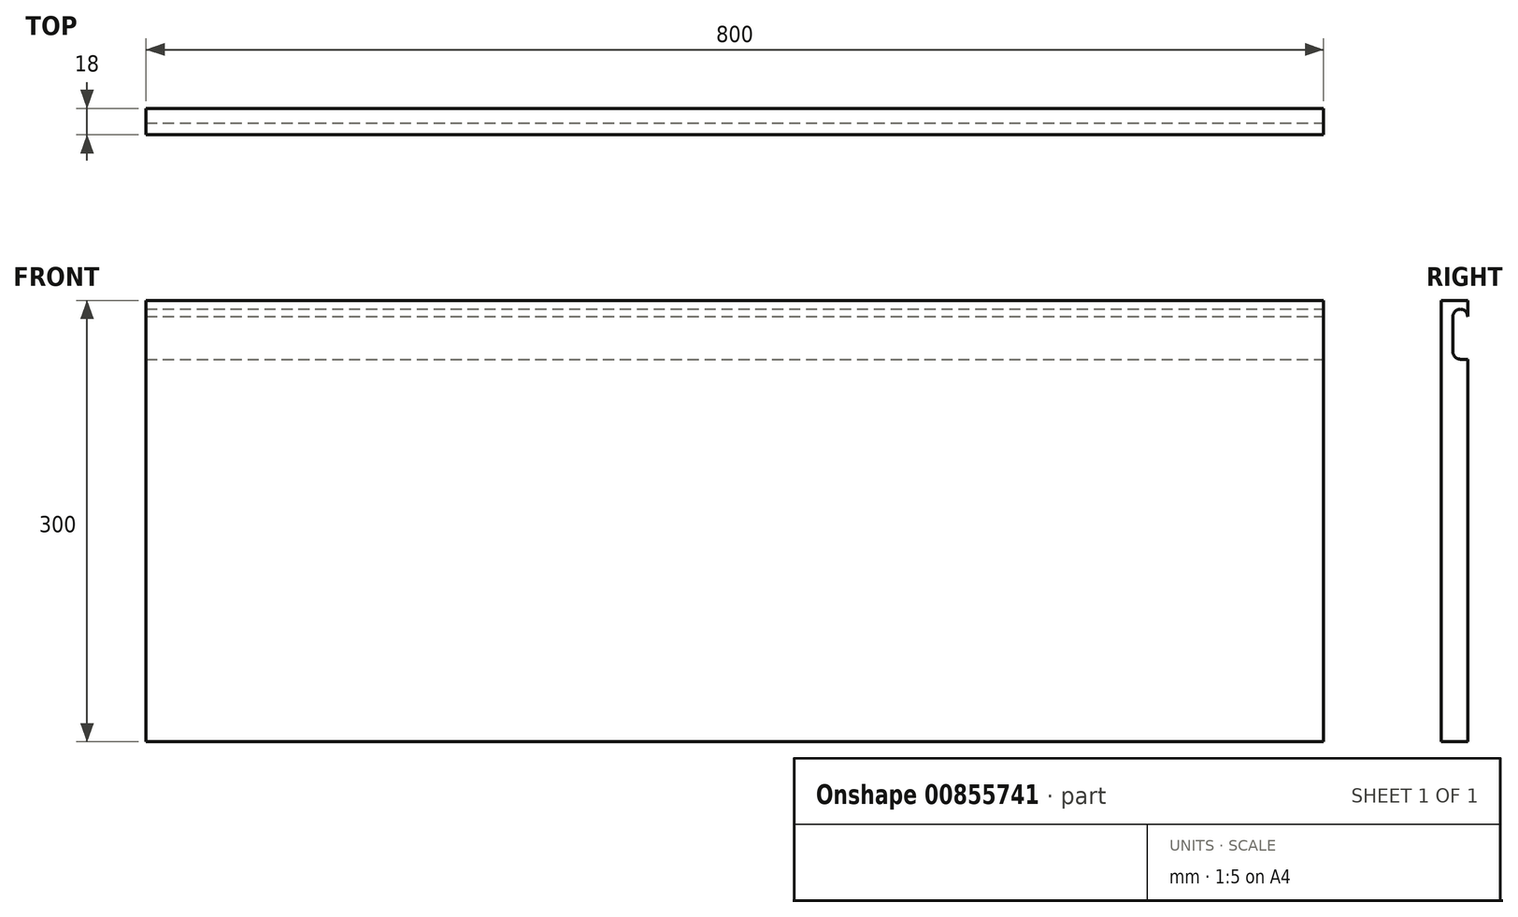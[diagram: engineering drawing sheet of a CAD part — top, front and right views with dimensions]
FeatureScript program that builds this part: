
annotation { "Feature Type Name" : "Feature", "Feature Type Description" : "" }
export const myFeature = defineFeature(function(context is Context, id is Id, definition is map)
    precondition{}
    {
        {
            var Q0;
            Q0=qCreatedBy(makeId("Front.planeOp"),FACE);
            var sketch = newSketch(context, id + "F0", { "sketchPlane" : qUnion([Q0])});
            skLineSegment(sketch, "E0.0", {"start": v(-303.71, 131.37) * mm, "end": v(-303.71, -87.91) * mm});
            skLineSegment(sketch, "E0.1", {"start": v(-303.71, -87.91) * mm, "end": v(-303.71, -150.63) * mm});
            skLineSegment(sketch, "E0.5", {"start": v(-303.71, 131.37) * mm, "end": v(53.29, 131.37) * mm});
            skLineSegment(sketch, "E1.1", {"start": v(460.29, 131.37) * mm, "end": v(460.29, -150.63) * mm});
            skLineSegment(sketch, "E1.2", {"start": v(53.29, 131.37) * mm, "end": v(460.29, 131.37) * mm});
            skLineSegment(sketch, "E2.bottom", {"start": v(-321.71, 149.37) * mm, "end": v(478.29, 149.37) * mm});
            skLineSegment(sketch, "E2.top", {"start": v(-321.71, -150.63) * mm, "end": v(-303.71, -150.63) * mm});
            skLineSegment(sketch, "E2.left", {"start": v(-321.71, 149.37) * mm, "end": v(-321.71, -150.63) * mm});
            skLineSegment(sketch, "E2.right", {"start": v(478.29, 149.37) * mm, "end": v(478.29, -150.63) * mm});
            skLineSegment(sketch, "E3", {"start": v(-303.71, -150.63) * mm, "end": v(478.29, -150.63) * mm});
            skSolve(sketch);
        }
        {
            var Q0;
            Q0=makeQuery(id+"F0.imprint","IMPRINT",FACE,{"disambiguationData":[TD([[makeQuery(id+"F0.imprint","IMPRINT",EDGE,{"derivedFrom":sQuery(id+"F0.wireOp",EDGE,"E0.0")}),1.0]])]});
            var Q1;
            Q1=makeQuery(id+"F0.imprint","IMPRINT",FACE,{"disambiguationData":[TD([[makeQuery(id+"F0.imprint","IMPRINT",EDGE,{"derivedFrom":sQuery(id+"F0.wireOp",EDGE,"E0.0")}),-1.0]])]});
            extrude(context, id + "F1", {"entities" : qUnion([Q0, Q1]), "oppositeDirection" : true, "depth" : 18 * mm, "offsetDistance" : 25 * mm});
        }
        {
            var Q0;
            Q0=makeQuery(id+"F1.opExtrude","SWEPT_FACE",FACE,{"disambiguationData":[OSD([sQuery(id+"F0.wireOp",EDGE,"E2.right")])]});
            var sketch = newSketch(context, id + "F2", { "sketchPlane" : qUnion([Q0])});
            skLineSegment(sketch, "E4", {"start": v(18, 109.37) * mm, "end": v(13, 109.37) * mm});
            skLineSegment(sketch, "E5", {"start": v(8, 114.37) * mm, "end": v(8, 138.37) * mm});
            skArc(sketch, "E6", {"start": v(18, 138.37) * mm, "mid": v(13, 143.37) * mm, "end": v(8, 138.37) * mm});
            skPoint(sketch, "E7.visualSharp", {"position": v(8, 109.37) * mm});
            skArc(sketch, "E7.filletArc", {"start": v(8, 114.37) * mm, "mid": v(9.46, 110.84) * mm, "end": v(13, 109.37) * mm});
            skSolve(sketch);
        }
        {
            var Q0;
            Q0 = qSketchRegion(id + "F2", true);
            var Q1;
            {var subQ1=sQuery(id+"F2.wireOp",EDGE,"E4");Q1=makeQuery(id+"F2.imprint","IMPRINT",FACE,{"disambiguationData":[TD([[makeQuery(id+"F2.imprint","IMPRINT",EDGE,{"derivedFrom":subQ1}),-1.0]])]});}
            extrude(context, id + "F3", {"entities" : qUnion([Q0, Q1]), "operationType" : NewBodyOperationType.REMOVE, "oppositeDirection" : true, "depth" : 906 * mm, "offsetDistance" : 25 * mm});
        }
    });
